# Revit family: Haworth_GranTorino_Sofa_TwoSeat
name_source: partatom
category: Furniture
revit_build: Autodesk Revit 2018 (Build: 20170223_1515(x64)
units: mm (PartAtom-declared; Revit-internal decimal feet)

## family parameters
Always vertical = Yes
Cut with Voids When Loaded = No
OmniClass Number = 23.40.20.00
OmniClass Title = General Furniture and Specialties
Room Calculation Point = No
Shared = No
Work Plane-Based = No

## types (2) — shared parameters
Actual Depth = 2' - 10 1/4"
Actual Height = 4' - 1 11/16"
Assembly Code = E2020200
Cushion Depth = 2' - 7 1/4"
Description = Haworth GranTorino HB Two Seat Sofa
Leg Finish = Haworth _ Metal _ Brushed Aluminum
Manufacturer = Haworth
Model = HCPF-GHL2
Size = Verify Final Dim. w/ Haworth
URL = http://www.haworth.com
URL - Product = http://www.haworth.com
Version = 2
Warranty = http://www.haworth.com

## per-type parameters (varying)
| type | Actual Width | Long | Outer Back End Screen Width | Short |
| HCPF-GHL2 - Long | 7' - 3 1/2" | Yes | 3' - 7" | No |
| HCPF-GHL2 - Short | 5' - 11 3/4" | No | 2' - 11 1/8" | Yes |

## geometry (parser evidence)
native form markers: Blend x8, Sweep x13
no freeform markers — native parametric forms only
